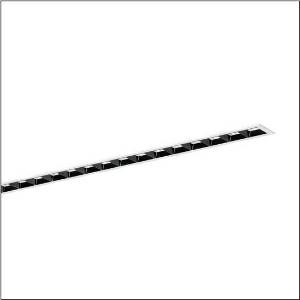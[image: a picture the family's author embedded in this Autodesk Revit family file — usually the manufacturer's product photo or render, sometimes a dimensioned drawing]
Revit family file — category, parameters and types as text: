
# Revit family: silica_r__21_51mx14da34wb_b271
name_source: partatom
category: Lighting Fixtures
units: mm (PartAtom-declared; Revit-internal decimal feet)

## family parameters
Cut with Voids When Loaded = No
Host = Face
Light Source = No
Part Type = Normal
Room Calculation Point = No
Round Connector Dimension = Use Diameter
Shared = No

## types (1)
- --- (1 x LED, 4320 lm, 32.1 W, 3000K)
    Apparent Load = 32 VA
    CIE Flux Codes = 74 94 99 100 100
    Color Rendering = 80
    Color Temperature = 3000K
    Default Elevation = 1800 mm
    Description = Silica® 21, office luminaire, primary light control with darklight reflector, of PMMA, black, light emission: direct distribution, primary light characteristic: asymmetric, installation type: recessed, LED, rated luminous flux: 4.320lm, luminous efficacy: 135lm/W, light colour: 830, colour temperature: 3000K, control gear: DALI 2, with terminal, 3+2-pole, max. 2.5mm², mains connection: 220..240V, AC, 50/60Hz, rated input power: 32.1W, luminaire housing, of aluminium, traffic white (RAL 9016), length: 1.228mm, width: 79mm, height: 53mm, protection rating (complete): IP20, insulation class (complete): insulation class I (protective earthing), certification: CE, ENEC, VDE, permissible operating ambient temperature: 0..+35°C, standard: EN 50419, packaging unit: 1 piece
    Height = 0 mm  [stored 0 ft]
    Lamp = 1 x LED
    Lamp Light Flux = 4320 lm
    Lamp Power = 32.1 W
    Lamp count = 1
    Length = 1227 mm
    Luminous efficacy = 135 lm/W
    Manufacturer = Siteco
    ModVariant = No
    Model = 51MX14DA34WB
    Mounting Place = Ceiling
    Mounting Type = Recessed
    Number of Poles = 1
    OnlyDefault = Yes
    Power Factor = 1
    Product Name = Silica® 21
    Product group = office luminaire | ceiling recessed
    ProductGroupID = 401
    Protection Class = Protection class I
    Protection Degree = IP 20
    RLX_Detail_Level = 1
    RLX_Emergency_Light_Flux = 0 lm
    RLX_Emergency_Type = 0
    RLX_Emergency_Type_DB = No
    RlxData = <blob elided: 39309 chars, md5=093a82f7>
    Socket = socket
    Standby Power = 0 W
    System Light Flux = 4320 lm
    System Power = 32 W
    Type Comments = factory setting: luminous flux: 100 % | dim-lin: 254 | 448 mA
    Type Image = l_1335880.jpg
    URL = http://relux.com
    VarID = @adj_122488
    Voltage = 0 V
    Weight = 0.00 kg
    Width = 79 mm

note: [stored X ft] marks values corroborated as IEEE doubles in the binary element streams (Revit-internal decimal feet)

## geometry (parser evidence)
native form markers: Blend x4, Sweep x11
no freeform markers — native parametric forms only
